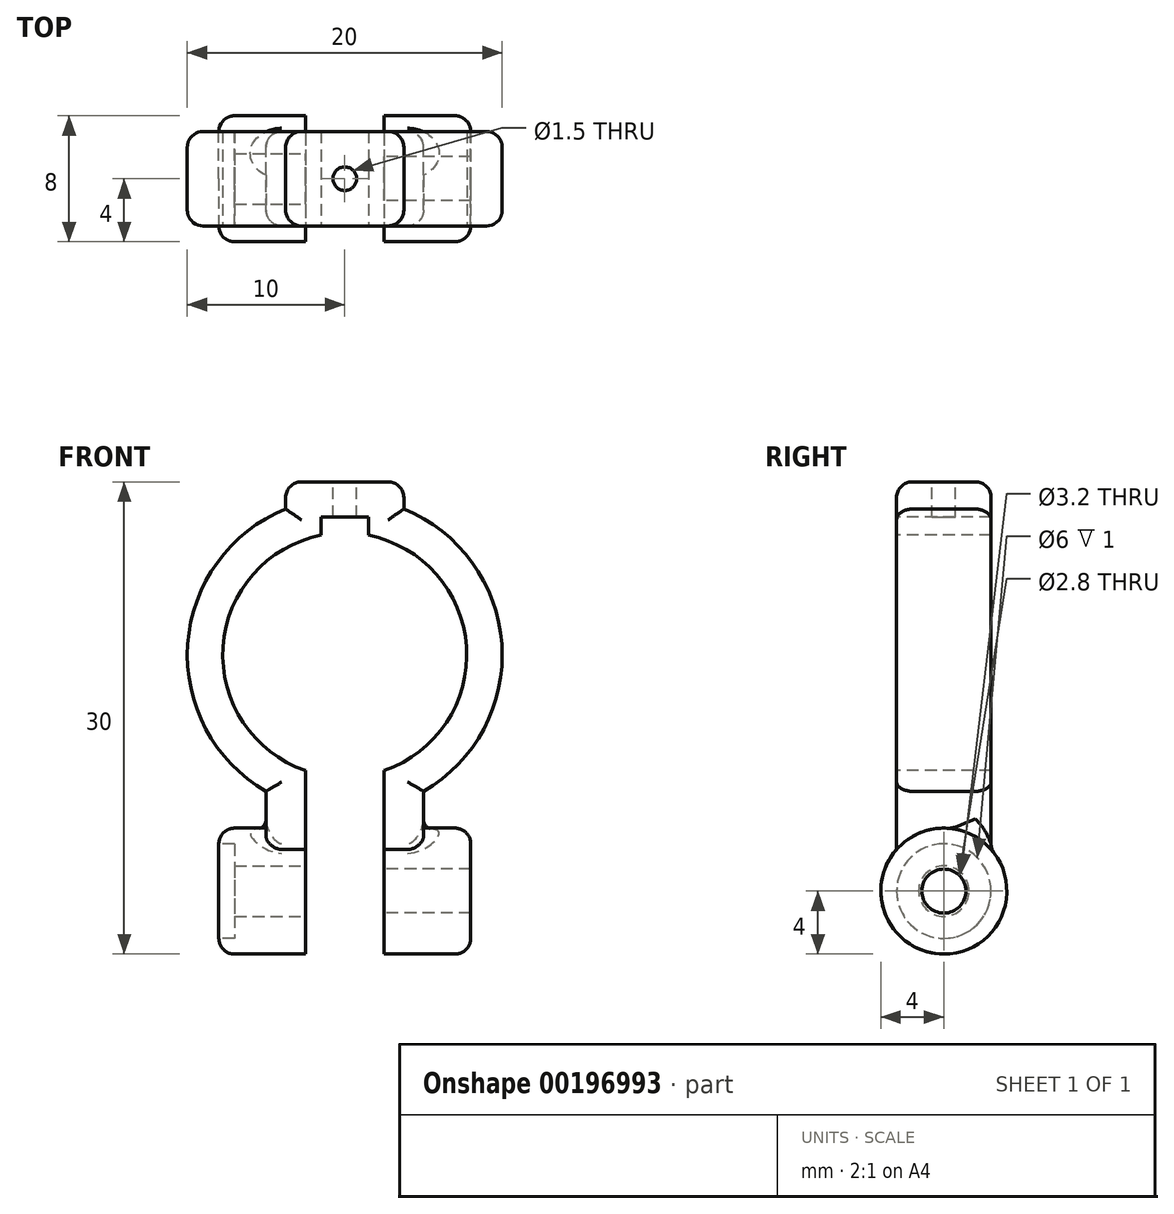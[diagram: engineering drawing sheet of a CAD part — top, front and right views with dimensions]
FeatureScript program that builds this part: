
annotation { "Feature Type Name" : "Feature", "Feature Type Description" : "" }
export const myFeature = defineFeature(function(context is Context, id is Id, definition is map)
    precondition{}
    {
        {
            var Q0;
            Q0=qCreatedBy(makeId("Front.planeOp"),FACE);
            var sketch = newSketch(context, id + "F0", { "sketchPlane" : qUnion([Q0])});
            skCircle(sketch, "E0", {"center": v(0, 0) * mm, "radius": 10 * mm});
            skSolve(sketch);
        }
        {
            var Q0;
            Q0 = qSketchRegion(id + "F0", true);
            extrude(context, id + "F1", {"entities" : qUnion([Q0]), "depth" : 5 * mm, "hasSecondDirection" : true, "secondDirectionOppositeDirection" : true, "secondDirectionDepth" : 1 * mm});
        }
        {
            var Q0;
            Q0=makeQuery(id+"F1.opExtrude","CAP_FACE",FACE,{"disambiguationData":[OSD([sQuery(id+"F0.wireOp",EDGE,"E0")])],"isStart":false});
            var sketch = newSketch(context, id + "F2", { "sketchPlane" : qUnion([Q0])});
            skCircle(sketch, "E1", {"center": v(0, 0) * mm, "radius": 7.75 * mm});
            skSolve(sketch);
        }
        {
            var Q0;
            Q0 = qSketchRegion(id + "F2", true);
            extrude(context, id + "F3", {"entities" : qUnion([Q0]), "operationType" : NewBodyOperationType.REMOVE, "endBound" : BoundingType.THROUGH_ALL, "oppositeDirection" : true, "depth" : 25 * mm});
        }
        {
            var Q0;
            Q0=qCreatedBy(makeId("Right.planeOp"),FACE);
            var sketch = newSketch(context, id + "F4", { "sketchPlane" : qUnion([Q0])});
            skLineSegment(sketch, "E2.0", {"start": v(1, -10) * mm, "end": v(1, 10) * mm, "construction": true});
            skLineSegment(sketch, "E3.0", {"start": v(-5, -10) * mm, "end": v(-5, 10) * mm, "construction": true});
            skLineSegment(sketch, "E4", {"start": v(-5, -10) * mm, "end": v(1, -10) * mm, "construction": true});
            skLineSegment(sketch, "E5", {"start": v(-2, -10) * mm, "end": v(-2, -15) * mm, "construction": true});
            skCircle(sketch, "E6", {"center": v(-2, -15) * mm, "radius": 4 * mm});
            skSolve(sketch);
        }
        {
            var Q0;
            Q0 = qSketchRegion(id + "F4", true);
            extrude(context, id + "F5", {"entities" : qUnion([Q0]), "depth" : 8 * mm, "hasSecondDirection" : true, "secondDirectionOppositeDirection" : true, "secondDirectionDepth" : 8 * mm});
        }
        {
            var Q0;
            Q0=qCreatedBy(makeId("Front.planeOp"),FACE);
            var sketch = newSketch(context, id + "F6", { "sketchPlane" : qUnion([Q0])});
            skLineSegment(sketch, "E7", {"start": v(0, 0) * mm, "end": v(0, -7.75) * mm, "construction": true});
            skLineSegment(sketch, "E8.bottom", {"start": v(-5, -7.75) * mm, "end": v(5, -7.75) * mm});
            skLineSegment(sketch, "E8.top", {"start": v(-5, -15) * mm, "end": v(5, -15) * mm});
            skLineSegment(sketch, "E8.left", {"start": v(-5, -7.75) * mm, "end": v(-5, -15) * mm});
            skLineSegment(sketch, "E8.right", {"start": v(5, -7.75) * mm, "end": v(5, -15) * mm});
            skLineSegment(sketch, "E9.0", {"start": v(-8, -11) * mm, "end": v(-8, -19) * mm, "construction": true});
            skLineSegment(sketch, "E10", {"start": v(-8, -15) * mm, "end": v(-5, -15) * mm, "construction": true});
            skSolve(sketch);
        }
        {
            var Q0;
            Q0 = qSketchRegion(id + "F6", true);
            extrude(context, id + "F7", {"entities" : qUnion([Q0]), "operationType" : NewBodyOperationType.ADD, "depth" : 5 * mm, "hasSecondDirection" : true, "secondDirectionOppositeDirection" : true, "secondDirectionDepth" : 1 * mm});
        }
        {
            var Q0;
            Q0=qCreatedBy(makeId("Front.planeOp"),FACE);
            var sketch = newSketch(context, id + "F8", { "sketchPlane" : qUnion([Q0])});
            skLineSegment(sketch, "E11.bottom", {"start": v(-2.5, 0) * mm, "end": v(2.5, 0) * mm});
            skLineSegment(sketch, "E11.top", {"start": v(-2.5, -25.02) * mm, "end": v(2.5, -25.02) * mm});
            skLineSegment(sketch, "E11.left", {"start": v(-2.5, 0) * mm, "end": v(-2.5, -25.02) * mm});
            skLineSegment(sketch, "E11.right", {"start": v(2.5, 0) * mm, "end": v(2.5, -25.02) * mm});
            skSolve(sketch);
        }
        {
            var Q0;
            Q0 = qSketchRegion(id + "F8", true);
            extrude(context, id + "F9", {"entities" : qUnion([Q0]), "operationType" : NewBodyOperationType.REMOVE, "endBound" : BoundingType.THROUGH_ALL, "oppositeDirection" : true, "depth" : 25 * mm, "hasSecondDirection" : true, "secondDirectionBound" : BoundingType.THROUGH_ALL, "secondDirectionOppositeDirection" : false, "secondDirectionDepth" : 25 * mm});
        }
        {
            var Q0;
            Q0=qCreatedBy(makeId("Right.planeOp"),FACE);
            var sketch = newSketch(context, id + "F10", { "sketchPlane" : qUnion([Q0])});
            skCircle(sketch, "E12.0", {"center": v(-2, -15) * mm, "radius": 4 * mm, "construction": true});
            skCircle(sketch, "E13", {"center": v(-2, -15) * mm, "radius": 1.6 * mm});
            skSolve(sketch);
        }
        {
            var Q0;
            Q0 = qSketchRegion(id + "F10", true);
            extrude(context, id + "F11", {"entities" : qUnion([Q0]), "operationType" : NewBodyOperationType.REMOVE, "endBound" : BoundingType.THROUGH_ALL, "oppositeDirection" : true, "depth" : 25 * mm});
        }
        {
            var Q0;
            Q0=makeQuery(id+"F5.opExtrude","CAP_FACE",FACE,{"disambiguationData":[OSD([sQuery(id+"F4.wireOp",EDGE,"E6")])],"isStart":true});
            var sketch = newSketch(context, id + "F12", { "sketchPlane" : qUnion([Q0])});
            skCircle(sketch, "E14", {"center": v(2, -15) * mm, "radius": 3 * mm});
            skSolve(sketch);
        }
        {
            var Q0;
            Q0 = qSketchRegion(id + "F12", true);
            extrude(context, id + "F13", {"entities" : qUnion([Q0]), "operationType" : NewBodyOperationType.REMOVE, "oppositeDirection" : true, "depth" : 1 * mm});
        }
        {
            var Q0;
            Q0=qCreatedBy(makeId("Right.planeOp"),FACE);
            var sketch = newSketch(context, id + "F14", { "sketchPlane" : qUnion([Q0])});
            skCircle(sketch, "E15.0", {"center": v(-2, -15) * mm, "radius": 4 * mm, "construction": true});
            skCircle(sketch, "E16", {"center": v(-2, -15) * mm, "radius": 1.4 * mm});
            skSolve(sketch);
        }
        {
            var Q0;
            Q0 = qSketchRegion(id + "F14", true);
            extrude(context, id + "F15", {"entities" : qUnion([Q0]), "operationType" : NewBodyOperationType.REMOVE, "endBound" : BoundingType.THROUGH_ALL, "depth" : 25 * mm});
        }
        {
            var Q0;
            Q0=makeQuery(id+"F7.boolean.opBoolean","MERGE",FACE,{"derivedFrom":[makeQuery(id+"F1.opExtrude","CAP_FACE",FACE,{"disambiguationData":[OSD([sQuery(id+"F0.wireOp",EDGE,"E0")])],"isStart":false}),makeQuery(id+"F7.opExtrude","CAP_FACE",FACE,{"disambiguationData":[OSD([sQuery(id+"F6.wireOp",EDGE,"E8.bottom"),sQuery(id+"F6.wireOp",EDGE,"E8.top"),sQuery(id+"F6.wireOp",EDGE,"E8.left"),sQuery(id+"F6.wireOp",EDGE,"E8.right")])],"isStart":false})]});
            var sketch = newSketch(context, id + "F16", { "sketchPlane" : qUnion([Q0])});
            skLineSegment(sketch, "E17", {"start": v(0, 0) * mm, "end": v(0, 7.75) * mm, "construction": true});
            skLineSegment(sketch, "E18.bottom", {"start": v(1.5, 8.75) * mm, "end": v(-1.5, 8.75) * mm});
            skLineSegment(sketch, "E18.top", {"start": v(1.5, 6.75) * mm, "end": v(-1.5, 6.75) * mm});
            skLineSegment(sketch, "E18.left", {"start": v(1.5, 8.75) * mm, "end": v(1.5, 6.75) * mm});
            skLineSegment(sketch, "E18.right", {"start": v(-1.5, 8.75) * mm, "end": v(-1.5, 6.75) * mm});
            skPoint(sketch, "E18.middle", {"position": v(0, 7.75) * mm});
            skSolve(sketch);
        }
        {
            var Q0;
            Q0 = qSketchRegion(id + "F16", true);
            extrude(context, id + "F17", {"entities" : qUnion([Q0]), "operationType" : NewBodyOperationType.REMOVE, "endBound" : BoundingType.THROUGH_ALL, "oppositeDirection" : true, "depth" : 25 * mm});
        }
        {
            var Q0;
            Q0=makeQuery(id+"F7.boolean.opBoolean","MERGE",FACE,{"derivedFrom":[makeQuery(id+"F1.opExtrude","CAP_FACE",FACE,{"disambiguationData":[OSD([sQuery(id+"F0.wireOp",EDGE,"E0")])],"isStart":false}),makeQuery(id+"F7.opExtrude","CAP_FACE",FACE,{"disambiguationData":[OSD([sQuery(id+"F6.wireOp",EDGE,"E8.bottom"),sQuery(id+"F6.wireOp",EDGE,"E8.top"),sQuery(id+"F6.wireOp",EDGE,"E8.left"),sQuery(id+"F6.wireOp",EDGE,"E8.right")])],"isStart":false})]});
            var sketch = newSketch(context, id + "F18", { "sketchPlane" : qUnion([Q0])});
            skLineSegment(sketch, "E19.0", {"start": v(0, 0) * mm, "end": v(0, 7.75) * mm, "construction": true});
            skLineSegment(sketch, "E19.1", {"start": v(1.5, 8.75) * mm, "end": v(-1.5, 8.75) * mm, "construction": true});
            skLineSegment(sketch, "E19.2", {"start": v(1.5, 6.75) * mm, "end": v(-1.5, 6.75) * mm, "construction": true});
            skLineSegment(sketch, "E19.3", {"start": v(1.5, 8.75) * mm, "end": v(1.5, 6.75) * mm, "construction": true});
            skLineSegment(sketch, "E19.4", {"start": v(-1.5, 8.75) * mm, "end": v(-1.5, 6.75) * mm, "construction": true});
            skPoint(sketch, "E19.5", {"position": v(0, 7.75) * mm});
            skLineSegment(sketch, "E20.0", {"start": v(-3.75, 11) * mm, "end": v(-3.75, 6.75) * mm});
            skLineSegment(sketch, "E20.1", {"start": v(3.75, 11) * mm, "end": v(-3.75, 11) * mm});
            skLineSegment(sketch, "E20.2", {"start": v(3.75, 11) * mm, "end": v(3.75, 6.75) * mm});
            skArc(sketch, "E21.0", {"start": v(-1.5, 7.6) * mm, "mid": v(-2.66, 7.28) * mm, "end": v(-3.75, 6.78) * mm});
            skArc(sketch, "E22.0", {"start": v(3.75, 6.78) * mm, "mid": v(2.66, 7.28) * mm, "end": v(1.5, 7.6) * mm});
            skPoint(sketch, "E23.orphan", {"position": v(-2.5, -7.34) * mm});
            skPoint(sketch, "E24.orphan", {"position": v(2.5, -7.34) * mm});
            skLineSegment(sketch, "E25", {"start": v(-1.5, 7.6) * mm, "end": v(-1.5, 8.75) * mm});
            skLineSegment(sketch, "E26", {"start": v(1.5, 8.75) * mm, "end": v(1.5, 7.6) * mm});
            skLineSegment(sketch, "E27", {"start": v(-1.5, 8.75) * mm, "end": v(1.5, 8.75) * mm});
            skSolve(sketch);
        }
        {
            var Q0;
            Q0 = qSketchRegion(id + "F18", true);
            var Q1;
            Q1=makeQuery(id+"F7.boolean.opBoolean","MERGE",FACE,{"derivedFrom":[makeQuery(id+"F1.opExtrude","CAP_FACE",FACE,{"disambiguationData":[OSD([sQuery(id+"F0.wireOp",EDGE,"E0")])],"isStart":true}),makeQuery(id+"F7.opExtrude","CAP_FACE",FACE,{"disambiguationData":[OSD([sQuery(id+"F6.wireOp",EDGE,"E8.bottom"),sQuery(id+"F6.wireOp",EDGE,"E8.top"),sQuery(id+"F6.wireOp",EDGE,"E8.left"),sQuery(id+"F6.wireOp",EDGE,"E8.right")])],"isStart":true})]});
            extrude(context, id + "F19", {"entities" : qUnion([Q0]), "operationType" : NewBodyOperationType.ADD, "endBound" : BoundingType.UP_TO_SURFACE, "oppositeDirection" : true, "endBoundEntityFace" : qUnion([Q1]), "depth" : 25 * mm});
        }
        {
            var Q0;
            Q0=makeQuery(id+"F19.opExtrude","SWEPT_FACE",FACE,{"disambiguationData":[OSD([sQuery(id+"F18.wireOp",EDGE,"E20.1")])]});
            var sketch = newSketch(context, id + "F20", { "sketchPlane" : qUnion([Q0])});
            skLineSegment(sketch, "E28", {"start": v(-3.75, 1) * mm, "end": v(3.75, -5) * mm, "construction": true});
            skCircle(sketch, "E29", {"center": v(0, -2) * mm, "radius": 0.75 * mm});
            skSolve(sketch);
        }
        {
            var Q0;
            Q0 = qSketchRegion(id + "F20", true);
            extrude(context, id + "F21", {"entities" : qUnion([Q0]), "operationType" : NewBodyOperationType.REMOVE, "endBound" : BoundingType.UP_TO_NEXT, "oppositeDirection" : true, "depth" : 25 * mm});
        }
        {
            var Q0;
            {var subQ0=sQuery(id+"F6.wireOp",EDGE,"E8.right");var subQ2=sQuery(id+"F0.wireOp",EDGE,"E0");Q0=makeQuery(id+"F19.boolean.opBoolean","SPLIT",EDGE,{"disambiguationData":[TD([makeQuery(id+"F7.opExtrude","SWEPT_FACE",FACE,{"disambiguationData":[OSD([subQ0])]})])],"derivedFrom":makeQuery(id+"F1.opExtrude","CAP_EDGE",EDGE,{"disambiguationData":[OSD([subQ2])],"isStart":false})});}
            var Q1;
            Q1=makeQuery(id+"F19.opExtrude","CAP_EDGE",EDGE,{"disambiguationData":[OSD([sQuery(id+"F18.wireOp",EDGE,"E20.2")])],"isStart":true});
            var Q2;
            Q2=makeQuery(id+"F19.opExtrude","CAP_EDGE",EDGE,{"disambiguationData":[OSD([sQuery(id+"F18.wireOp",EDGE,"E20.1")])],"isStart":true});
            var Q3;
            Q3=makeQuery(id+"F19.opExtrude","CAP_EDGE",EDGE,{"disambiguationData":[OSD([sQuery(id+"F18.wireOp",EDGE,"E20.0")])],"isStart":true});
            var Q4;
            {var subQ0=sQuery(id+"F6.wireOp",EDGE,"E8.left");var subQ1=sQuery(id+"F0.wireOp",EDGE,"E0");Q4=makeQuery(id+"F19.boolean.opBoolean","SPLIT",EDGE,{"disambiguationData":[TD([makeQuery(id+"F7.opExtrude","SWEPT_FACE",FACE,{"disambiguationData":[OSD([subQ0])]})])],"derivedFrom":makeQuery(id+"F1.opExtrude","CAP_EDGE",EDGE,{"disambiguationData":[OSD([subQ1])],"isStart":false})});}
            var Q5;
            Q5=makeQuery(id+"F7.opExtrude","CAP_EDGE",EDGE,{"disambiguationData":[OSD([sQuery(id+"F6.wireOp",EDGE,"E8.left")])],"isStart":false});
            var Q6;
            Q6=makeQuery(id+"F7.opExtrude","CAP_EDGE",EDGE,{"disambiguationData":[OSD([sQuery(id+"F6.wireOp",EDGE,"E8.right")])],"isStart":false});
            var Q7;
            {var subQ0=sQuery(id+"F6.wireOp",EDGE,"E8.right");var subQ1=sQuery(id+"F0.wireOp",EDGE,"E0");Q7=makeQuery(id+"F19.boolean.opBoolean","SPLIT",EDGE,{"disambiguationData":[TD([makeQuery(id+"F7.opExtrude","SWEPT_FACE",FACE,{"disambiguationData":[OSD([subQ0])]})])],"derivedFrom":makeQuery(id+"F1.opExtrude","CAP_EDGE",EDGE,{"disambiguationData":[OSD([subQ1])],"isStart":true})});}
            var Q8;
            Q8=makeQuery(id+"F19.opExtrude","CAP_EDGE",EDGE,{"disambiguationData":[OSD([sQuery(id+"F18.wireOp",EDGE,"E20.2")])],"isStart":false});
            var Q9;
            Q9=makeQuery(id+"F19.opExtrude","CAP_EDGE",EDGE,{"disambiguationData":[OSD([sQuery(id+"F18.wireOp",EDGE,"E20.1")])],"isStart":false});
            var Q10;
            Q10=makeQuery(id+"F19.opExtrude","CAP_EDGE",EDGE,{"disambiguationData":[OSD([sQuery(id+"F18.wireOp",EDGE,"E20.0")])],"isStart":false});
            var Q11;
            {var subQ0=sQuery(id+"F6.wireOp",EDGE,"E8.left");var subQ1=sQuery(id+"F0.wireOp",EDGE,"E0");Q11=makeQuery(id+"F19.boolean.opBoolean","SPLIT",EDGE,{"disambiguationData":[TD([makeQuery(id+"F7.opExtrude","SWEPT_FACE",FACE,{"disambiguationData":[OSD([subQ0])]})])],"derivedFrom":makeQuery(id+"F1.opExtrude","CAP_EDGE",EDGE,{"disambiguationData":[OSD([subQ1])],"isStart":true})});}
            var Q12;
            Q12=makeQuery(id+"F7.opExtrude","CAP_EDGE",EDGE,{"disambiguationData":[OSD([sQuery(id+"F6.wireOp",EDGE,"E8.left")])],"isStart":true});
            var Q13;
            Q13=makeQuery(id+"F7.opExtrude","CAP_EDGE",EDGE,{"disambiguationData":[OSD([sQuery(id+"F6.wireOp",EDGE,"E8.right")])],"isStart":true});
            var Q14;
            {var subQ0=sQuery(id+"F6.wireOp",EDGE,"E8.right");var subQ1=makeQuery(id+"F7.opExtrude","CAP_FACE",FACE,{"disambiguationData":[OSD([sQuery(id+"F6.wireOp",EDGE,"E8.bottom"),sQuery(id+"F6.wireOp",EDGE,"E8.top"),sQuery(id+"F6.wireOp",EDGE,"E8.left"),subQ0])],"isStart":true});var subQ2=makeQuery(id+"F5.opExtrude","SWEPT_FACE",FACE,{"disambiguationData":[OSD([sQuery(id+"F4.wireOp",EDGE,"E6")])]});Q14=makeQuery(id+"F9.boolean.opBoolean","SPLIT",EDGE,{"disambiguationData":[TD([makeQuery(id+"F7.opExtrude","SWEPT_FACE",FACE,{"disambiguationData":[OSD([subQ0])]})])],"derivedFrom":makeQuery(id+"F7.boolean.opBoolean","INTERSECT",EDGE,{"derivedFrom":[subQ2,subQ1]})});}
            var Q15;
            {var subQ0=sQuery(id+"F6.wireOp",EDGE,"E8.left");var subQ1=makeQuery(id+"F7.opExtrude","CAP_FACE",FACE,{"disambiguationData":[OSD([sQuery(id+"F6.wireOp",EDGE,"E8.bottom"),sQuery(id+"F6.wireOp",EDGE,"E8.top"),subQ0,sQuery(id+"F6.wireOp",EDGE,"E8.right")])],"isStart":true});var subQ2=makeQuery(id+"F5.opExtrude","SWEPT_FACE",FACE,{"disambiguationData":[OSD([sQuery(id+"F4.wireOp",EDGE,"E6")])]});Q15=makeQuery(id+"F9.boolean.opBoolean","SPLIT",EDGE,{"disambiguationData":[TD([makeQuery(id+"F7.opExtrude","SWEPT_FACE",FACE,{"disambiguationData":[OSD([subQ0])]})])],"derivedFrom":makeQuery(id+"F7.boolean.opBoolean","INTERSECT",EDGE,{"derivedFrom":[subQ2,subQ1]})});}
            var Q16;
            Q16=makeQuery(id+"F19.opExtrude","SWEPT_EDGE",EDGE,{"disambiguationData":[OSD([sQuery(id+"F18.wireOp",EDGE,"E20.0"),sQuery(id+"F18.wireOp",EDGE,"E20.1")])]});
            var Q17;
            Q17=makeQuery(id+"F19.opExtrude","SWEPT_EDGE",EDGE,{"disambiguationData":[OSD([sQuery(id+"F18.wireOp",EDGE,"E20.1"),sQuery(id+"F18.wireOp",EDGE,"E20.2")])]});
            var Q18;
            Q18=makeQuery(id+"F5.opExtrude","CAP_EDGE",EDGE,{"disambiguationData":[OSD([sQuery(id+"F4.wireOp",EDGE,"E6")])],"isStart":true});
            var Q19;
            Q19=makeQuery(id+"F5.opExtrude","CAP_EDGE",EDGE,{"disambiguationData":[OSD([sQuery(id+"F4.wireOp",EDGE,"E6")])],"isStart":false});
            fillet(context, id + "F22", {"entities" : qUnion([Q0, Q1, Q2, Q3, Q4, Q5, Q6, Q7, Q8, Q9, Q10, Q11, Q12, Q13, Q14, Q15, Q16, Q17, Q18, Q19]), "radius" : 1 * mm, "tangentPropagation" : true, "allowEdgeOverflow" : false});
        }
    });
